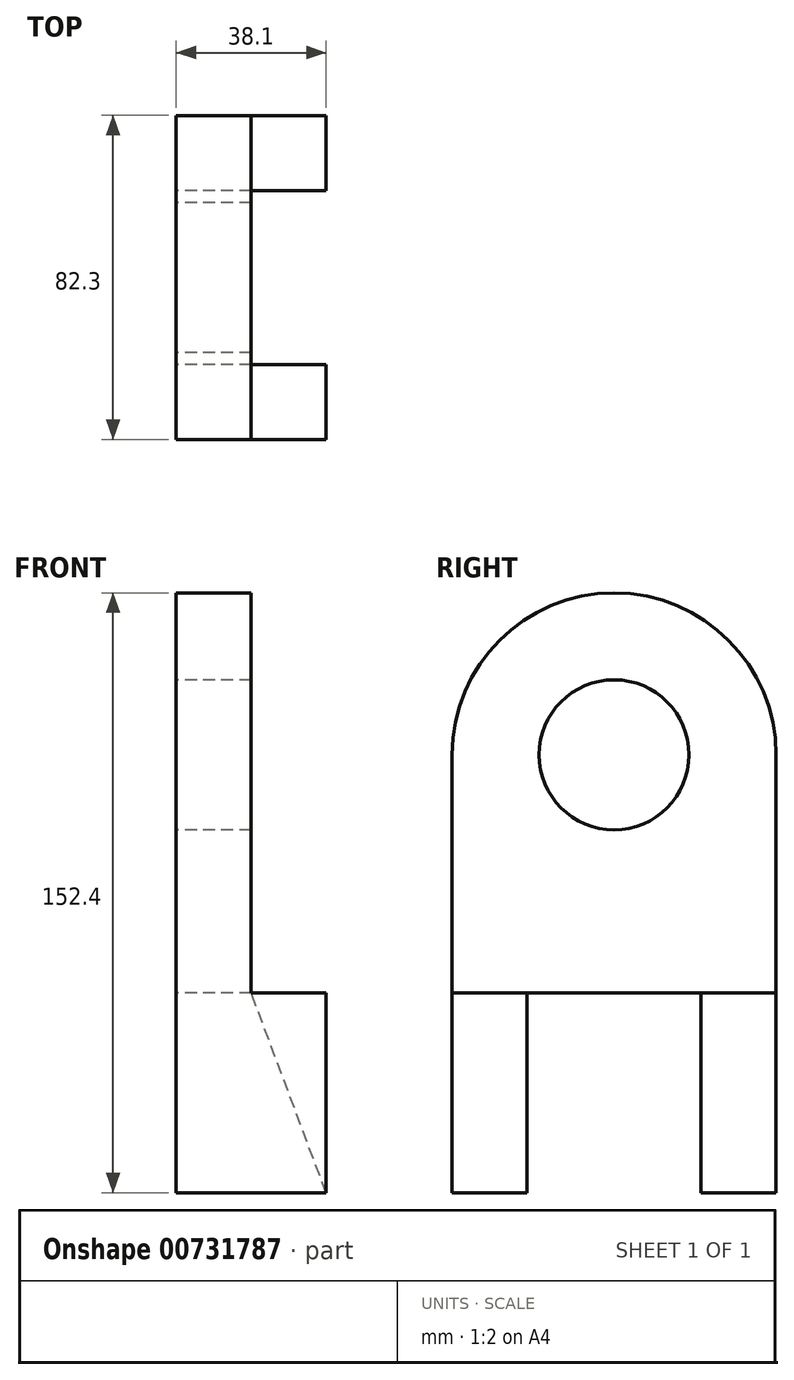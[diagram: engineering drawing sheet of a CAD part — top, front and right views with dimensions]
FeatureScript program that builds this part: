
annotation { "Feature Type Name" : "Feature", "Feature Type Description" : "" }
export const myFeature = defineFeature(function(context is Context, id is Id, definition is map)
    precondition{}
    {
        {
            var Q0;
            Q0=qCreatedBy(makeId("Right.planeOp"),FACE);
            var sketch = newSketch(context, id + "F0", { "sketchPlane" : qUnion([Q0])});
            skLineSegment(sketch, "E0", {"start": v(-41.15, 0) * mm, "end": v(-41.15, -111.25) * mm});
            skLineSegment(sketch, "E1", {"start": v(-41.15, -111.25) * mm, "end": v(-41.15, -111.25) * mm});
            skLineSegment(sketch, "E2", {"start": v(-22.1, -111.25) * mm, "end": v(-41.15, -111.25) * mm});
            skLineSegment(sketch, "E3", {"start": v(-22.1, -111.25) * mm, "end": v(-22.1, -60.45) * mm});
            skLineSegment(sketch, "E4", {"start": v(-22.1, -60.45) * mm, "end": v(-22.1, -60.45) * mm});
            skLineSegment(sketch, "E5", {"start": v(22.1, -60.45) * mm, "end": v(-22.1, -60.45) * mm});
            skLineSegment(sketch, "E6", {"start": v(22.1, -60.45) * mm, "end": v(22.1, -111.25) * mm});
            skLineSegment(sketch, "E7", {"start": v(22.1, -111.25) * mm, "end": v(22.1, -111.25) * mm});
            skLineSegment(sketch, "E8", {"start": v(41.15, -111.25) * mm, "end": v(22.1, -111.25) * mm});
            skLineSegment(sketch, "E9", {"start": v(41.15, -111.25) * mm, "end": v(41.15, 0) * mm});
            skLineSegment(sketch, "E10", {"start": v(41.15, 41.15) * mm, "end": v(41.15, 41.15) * mm});
            skLineSegment(sketch, "E11", {"start": v(0, 41.15) * mm, "end": v(0, 41.15) * mm});
            skPoint(sketch, "E12.visualSharp", {"position": v(-41.15, 41.15) * mm});
            skArc(sketch, "E12.filletArc", {"start": v(0, 41.15) * mm, "mid": v(-29.1, 29.1) * mm, "end": v(-41.15, 0) * mm});
            skPoint(sketch, "E13.visualSharp", {"position": v(41.15, 41.15) * mm});
            skArc(sketch, "E13.filletArc", {"start": v(41.15, 0) * mm, "mid": v(29.1, 29.1) * mm, "end": v(0, 41.15) * mm});
            skCircle(sketch, "E14", {"center": v(0, 0) * mm, "radius": 19.05 * mm});
            skSolve(sketch);
        }
        {
            var Q0;
            Q0 = qSketchRegion(id + "F0", true);
            extrude(context, id + "F1", {"entities" : qUnion([Q0]), "depth" : 19.05 * mm, "offsetDistance" : 25.4 * mm});
        }
        {
            var Q0;
            Q0=makeQuery(id+"F1.opExtrude","CAP_FACE",FACE,{"disambiguationData":[OSD([sQuery(id+"F0.wireOp",EDGE,"E0"),sQuery(id+"F0.wireOp",EDGE,"E2"),sQuery(id+"F0.wireOp",EDGE,"E3"),sQuery(id+"F0.wireOp",EDGE,"E5"),sQuery(id+"F0.wireOp",EDGE,"E6"),sQuery(id+"F0.wireOp",EDGE,"E8"),sQuery(id+"F0.wireOp",EDGE,"E9"),sQuery(id+"F0.wireOp",EDGE,"E12.filletArc"),sQuery(id+"F0.wireOp",EDGE,"E13.filletArc"),sQuery(id+"F0.wireOp",EDGE,"E14")])],"isStart":false});
            var sketch = newSketch(context, id + "F2", { "sketchPlane" : qUnion([Q0])});
            skLineSegment(sketch, "E15.bottom", {"start": v(-22.1, -60.45) * mm, "end": v(-41.15, -60.45) * mm});
            skLineSegment(sketch, "E15.top", {"start": v(-22.1, -111.25) * mm, "end": v(-41.15, -111.25) * mm});
            skLineSegment(sketch, "E15.left", {"start": v(-22.1, -60.45) * mm, "end": v(-22.1, -111.25) * mm});
            skLineSegment(sketch, "E15.right", {"start": v(-41.15, -60.45) * mm, "end": v(-41.15, -111.25) * mm});
            skSolve(sketch);
        }
        {
            var Q0;
            Q0=makeQuery(id+"F2.imprint","IMPRINT",FACE,{"disambiguationData":[TD([[makeQuery(id+"F2.imprint","IMPRINT",EDGE,{"derivedFrom":sQuery(id+"F2.wireOp",EDGE,"E15.bottom")}),1.0]])]});
            extrude(context, id + "F3", {"entities" : qUnion([Q0]), "operationType" : NewBodyOperationType.ADD, "depth" : 19.05 * mm, "offsetDistance" : 25.4 * mm});
        }
        {
            var Q0;
            Q0=makeQuery(id+"F1.opExtrude","SWEPT_FACE",FACE,{"disambiguationData":[OSD([sQuery(id+"F0.wireOp",EDGE,"E9")])]});
            var sketch = newSketch(context, id + "F4", { "sketchPlane" : qUnion([Q0])});
            skLineSegment(sketch, "E16", {"start": v(-38.1, -111.25) * mm, "end": v(-19.05, -60.45) * mm});
            skLineSegment(sketch, "E17", {"start": v(-19.05, -60.45) * mm, "end": v(-19.05, -60.45) * mm});
            skLineSegment(sketch, "E18", {"start": v(-19.05, -111.25) * mm, "end": v(-19.05, -60.45) * mm});
            skLineSegment(sketch, "E19", {"start": v(-19.05, -111.25) * mm, "end": v(-38.1, -111.25) * mm});
            skSolve(sketch);
        }
        {
            var Q0;
            Q0 = qSketchRegion(id + "F4", true);
            extrude(context, id + "F5", {"entities" : qUnion([Q0]), "operationType" : NewBodyOperationType.ADD, "oppositeDirection" : true, "depth" : 19.05 * mm, "offsetDistance" : 25.4 * mm});
        }
    });
